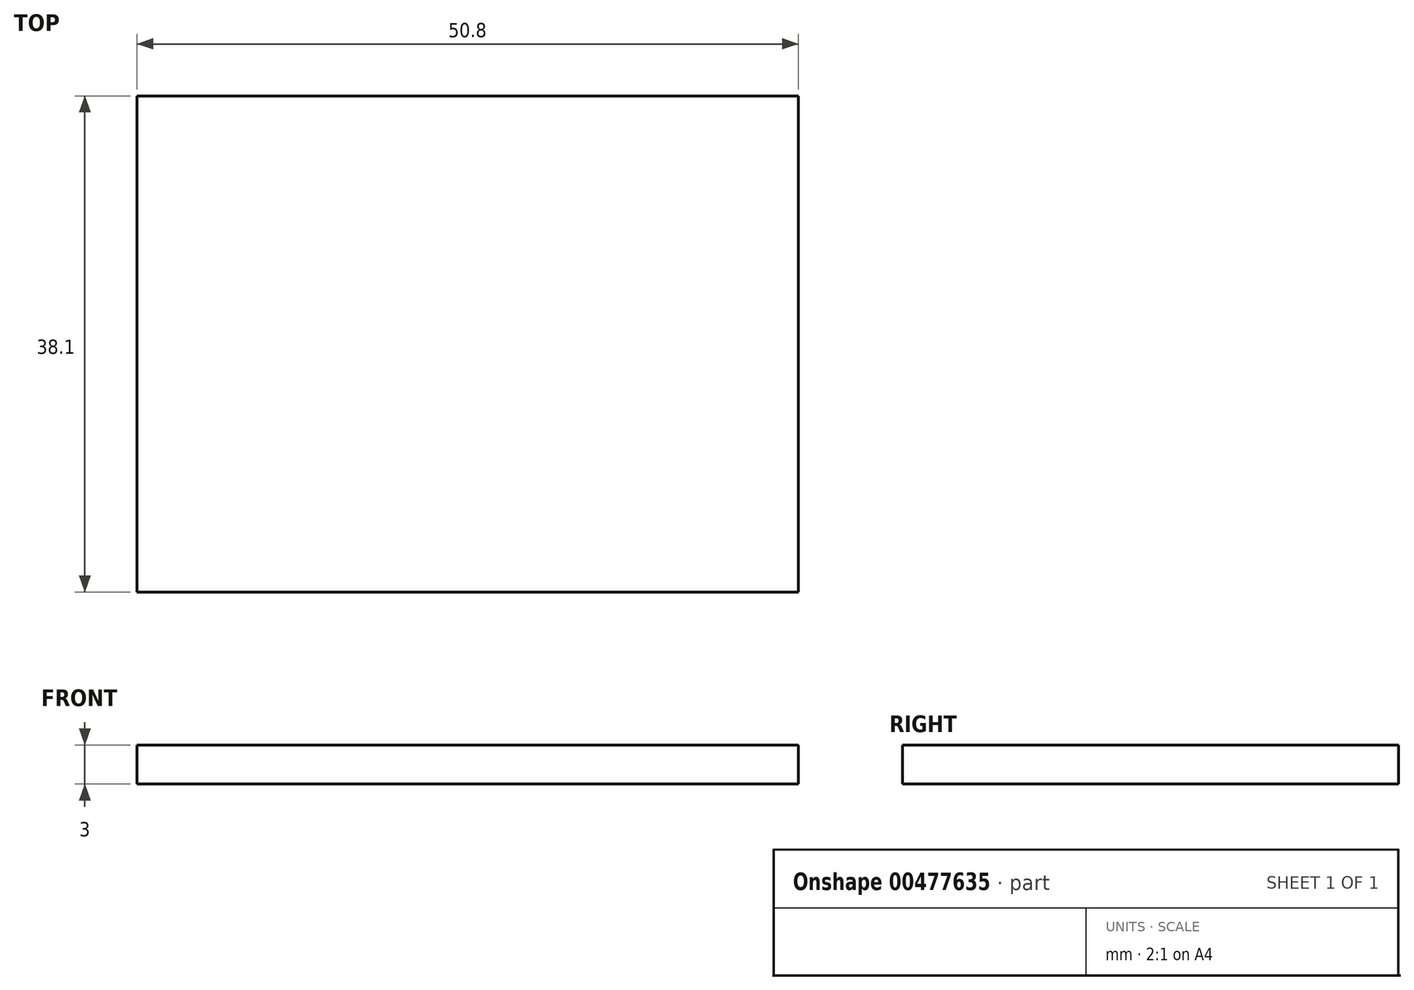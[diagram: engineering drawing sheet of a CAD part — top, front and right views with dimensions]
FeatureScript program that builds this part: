
annotation { "Feature Type Name" : "Feature", "Feature Type Description" : "" }
export const myFeature = defineFeature(function(context is Context, id is Id, definition is map)
    precondition{}
    {
        {
            var Q0;
            Q0=qCreatedBy(makeId("Top.planeOp"),FACE);
            var sketch = newSketch(context, id + "F0", { "sketchPlane" : qUnion([Q0])});
            skLineSegment(sketch, "E0.bottom", {"start": v(-26, 25.02) * mm, "end": v(24.8, 25.02) * mm});
            skLineSegment(sketch, "E0.top", {"start": v(-26, -13.08) * mm, "end": v(24.8, -13.08) * mm});
            skLineSegment(sketch, "E0.left", {"start": v(-26, 25.02) * mm, "end": v(-26, -13.08) * mm});
            skLineSegment(sketch, "E0.right", {"start": v(24.8, 25.02) * mm, "end": v(24.8, -13.08) * mm});
            skSolve(sketch);
        }
        {
            var Q0;
            Q0 = qSketchRegion(id + "F0", true);
            extrude(context, id + "F1", {"entities" : qUnion([Q0]), "depth" : 3 * mm});
        }
    });
